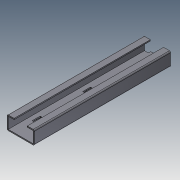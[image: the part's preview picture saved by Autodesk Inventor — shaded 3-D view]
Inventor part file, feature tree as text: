
AUTODESK INVENTOR PART (.ipt)
format: ipt  version: 2015 (Build 190159000, 159)  size: 254,976 bytes
history: native  units: mm
features: sheet_metal_op x9, other x8, sketch x6, plane x2
ambient origin geometry x8: Origin, YZ Plane, XZ Plane, XY Plane, X Axis, Y Axis, Z Axis, Center Point
bodies: Solid1 (feature_tree)
feature tree (25):
  sheet_metal_op  "Face1"
  sheet_metal_op  "Flange1"
  sheet_metal_op  "Flange2"
  sheet_metal_op  "Flange3"
  sheet_metal_op  "Flange4"
  plane  "Work Plane4"
  plane  "Work Plane6"
  sketch  "Sketch1"  dims[d4=0.001mm]
  other  "Plate1"
  sketch  "Sketch2"  dims[d5=3.0mm]
  other  "Plate2"
  sheet_metal_op  "Bend1"
  sketch  "Sketch3"  dims[d6=0.001mm]
  other  "Plate3"
  sheet_metal_op  "Bend2"
  sketch  "Sketch4"  dims[d7=6.0mm]
  other  "Plate4"
  sheet_metal_op  "Bend3"
  sketch  "Sketch5"  dims[d8=0.001mm]
  other  "Plate5"
  sheet_metal_op  "Bend4"
  sketch  "Sketch6"  dims[d9=29.0mm d10=90.0deg d11=0.001mm d12=3.0mm d13=0.001mm d14=6.0mm d15=0.001mm d16=29.0mm d17=90.0deg d18=0.001mm d19=3.0mm d20=0.001mm d21=6.0mm d22=0.001mm d23=15.0mm d24=90.0deg d25=0.001mm d26=3.0mm d27=0.001mm d28=6.0mm d29=0.001mm d30=15.0mm d31=90.0deg d32=0.001mm d33=4.0mm d34=20.5mm d35=4.0mm d36=20.5mm d37=0.0mm d38=33.0mm d40=4.0mm d41=0.0mm d42=350.0mm d45=150.0mm d46=10.0mm d47=10.0mm d48=64.0mm d49=6.0mm d50=64.0mm d51=4.0mm d52=9.0mm d62=20.5mm d63=4.0mm d64=9.0mm d65=20.5mm d66=4.0mm d68=4.0mm d69=0.0mm d71=50.0mm d72=33.0mm d73=16.5mm d0=3.0mm]
  other  "FlatPattern"
  other  "Cut1"
  other  "FlatPatternExtrusion2"
